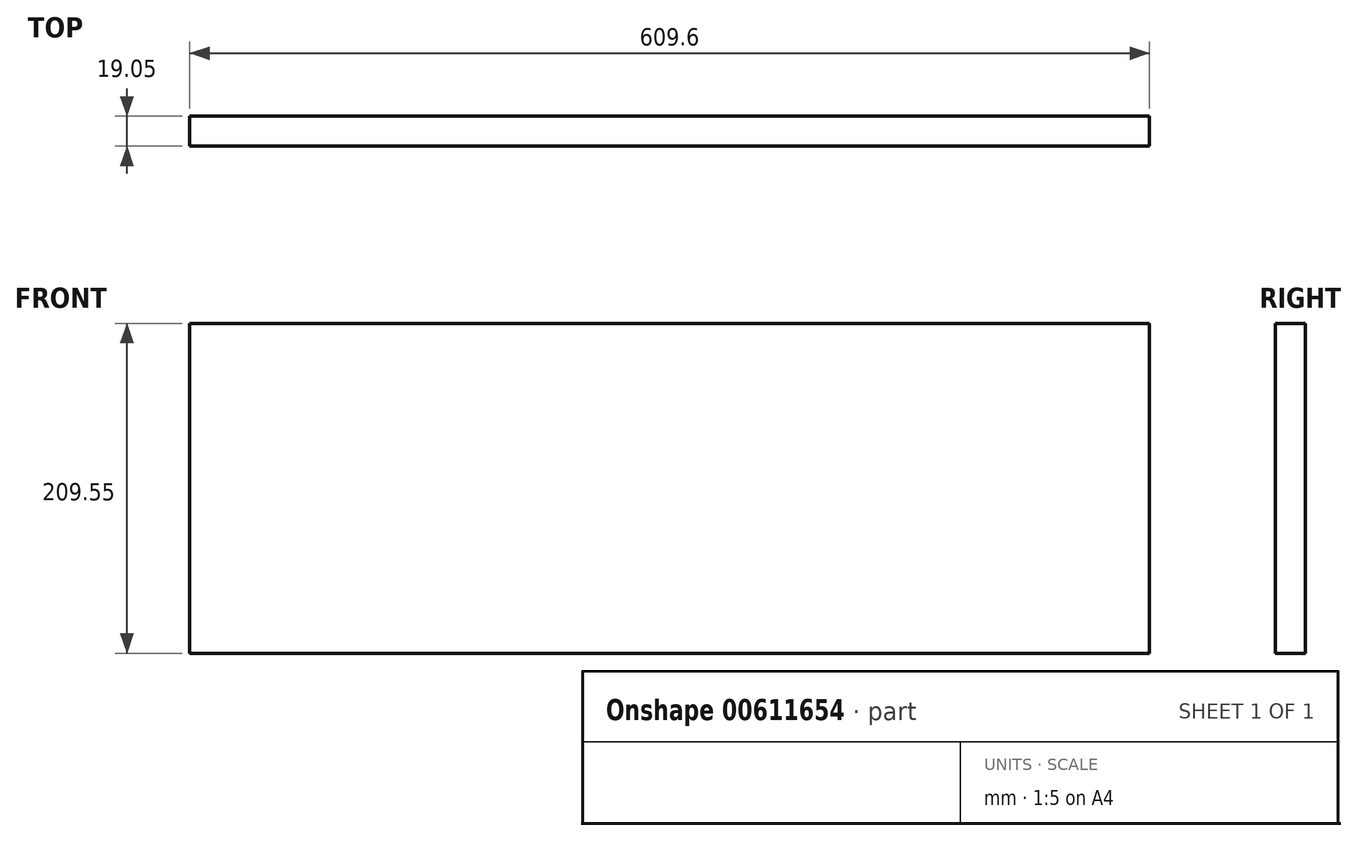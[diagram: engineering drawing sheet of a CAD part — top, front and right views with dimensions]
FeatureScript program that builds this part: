
annotation { "Feature Type Name" : "Feature", "Feature Type Description" : "" }
export const myFeature = defineFeature(function(context is Context, id is Id, definition is map)
    precondition{}
    {
        {
            var Q0;
            Q0=qCreatedBy(makeId("Front.planeOp"),FACE);
            var sketch = newSketch(context, id + "F0", { "sketchPlane" : qUnion([Q0])});
            skLineSegment(sketch, "E0", {"start": v(-306.9, 161.42) * mm, "end": v(302.7, 161.42) * mm});
            skLineSegment(sketch, "E1", {"start": v(302.7, 161.42) * mm, "end": v(302.7, -48.13) * mm});
            skLineSegment(sketch, "E2", {"start": v(302.7, -48.13) * mm, "end": v(-306.9, -48.13) * mm});
            skLineSegment(sketch, "E3", {"start": v(-306.9, -48.13) * mm, "end": v(-306.9, 161.42) * mm});
            skSolve(sketch);
        }
        {
            var Q0;
            Q0 = qSketchRegion(id + "F0", true);
            extrude(context, id + "F1", {"entities" : qUnion([Q0]), "depth" : 19.05 * mm, "offsetDistance" : 25.4 * mm});
        }
    });
